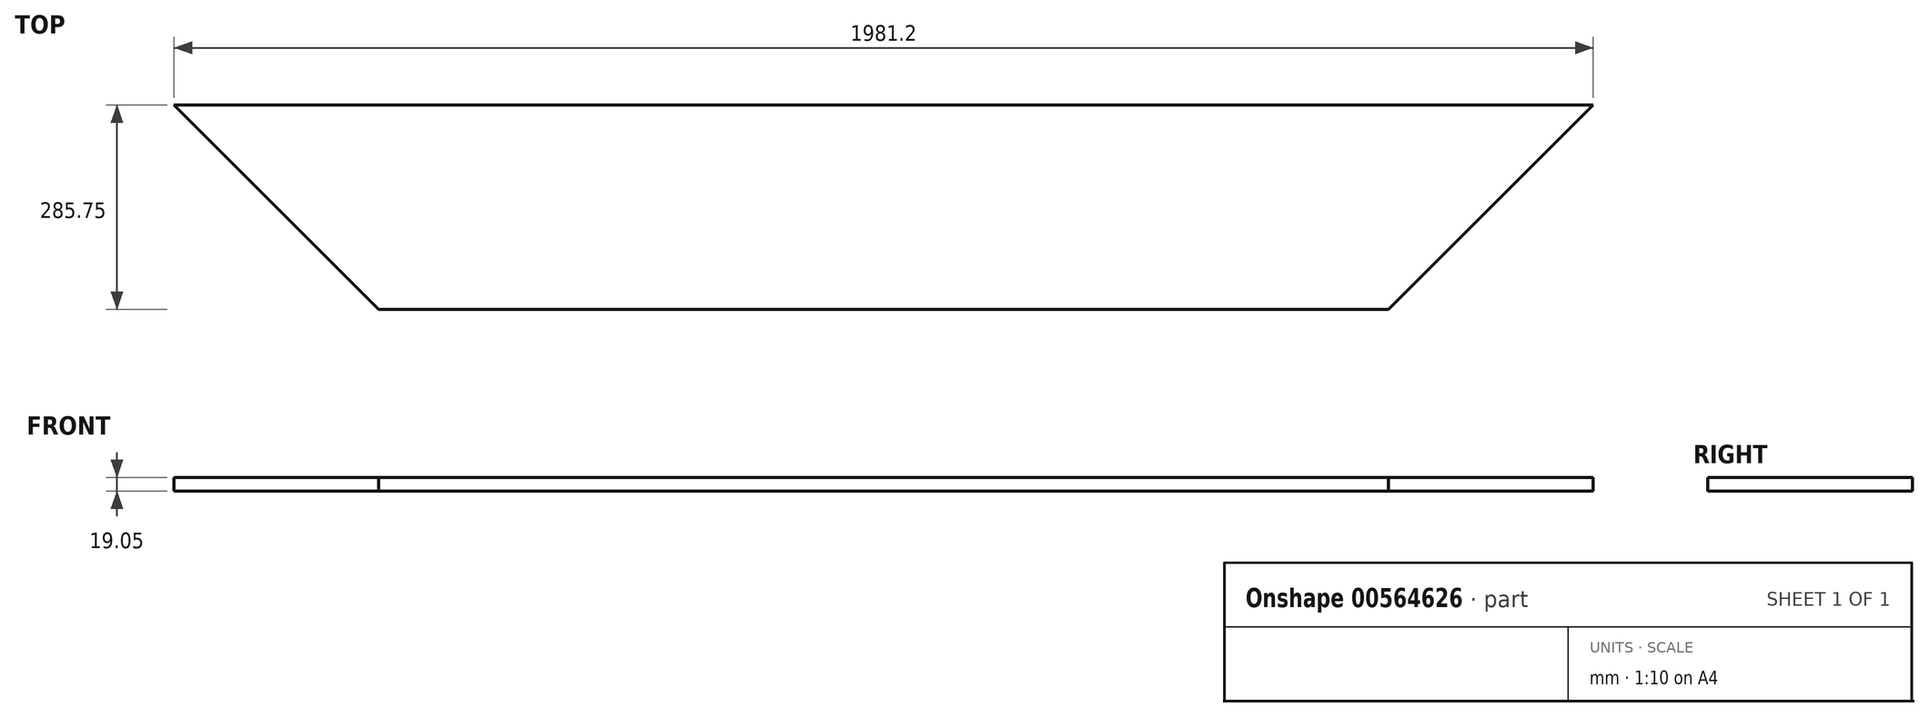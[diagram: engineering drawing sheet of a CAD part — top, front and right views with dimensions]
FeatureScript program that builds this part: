
annotation { "Feature Type Name" : "Feature", "Feature Type Description" : "" }
export const myFeature = defineFeature(function(context is Context, id is Id, definition is map)
    precondition{}
    {
        {
            var Q0;
            Q0=qCreatedBy(makeId("Top.planeOp"),FACE);
            var sketch = newSketch(context, id + "F0", { "sketchPlane" : qUnion([Q0])});
            skLineSegment(sketch, "E0", {"start": v(571.5, 0) * mm, "end": v(1981.2, 0) * mm});
            skLineSegment(sketch, "E1", {"start": v(2552.7, 0) * mm, "end": v(2266.95, 285.75) * mm, "construction": true});
            skLineSegment(sketch, "E2", {"start": v(2266.95, 285.75) * mm, "end": v(285.75, 285.75) * mm});
            skLineSegment(sketch, "E3", {"start": v(285.75, 285.75) * mm, "end": v(0, 0) * mm, "construction": true});
            skLineSegment(sketch, "E4", {"start": v(285.75, 285.75) * mm, "end": v(571.5, 0) * mm});
            skLineSegment(sketch, "E5", {"start": v(2266.95, 285.75) * mm, "end": v(1981.2, 0) * mm});
            skSolve(sketch);
        }
        {
            var Q0;
            Q0=makeQuery(id+"F0.imprint","IMPRINT",FACE,{"disambiguationData":[TD([[makeQuery(id+"F0.imprint","IMPRINT",EDGE,{"derivedFrom":sQuery(id+"F0.wireOp",EDGE,"E0")}),1.0]])]});
            extrude(context, id + "F1", {"entities" : qUnion([Q0]), "depth" : 19.05 * mm, "offsetDistance" : 25.4 * mm});
        }
    });
